# Revit family: Domotics-DomesticRanges-GEWISS-CHORUS_POWER-SOCKET-OUTLET_INDIA_SOUTHAFRICA
name_source: partatom
category: Apparecchi elettrici
revit_build: Autodesk Revit 2016 (Build: 20161004_0715(x64)
units: mm (PartAtom-declared; Revit-internal decimal feet)

## family parameters
Condiviso = Sì
Host = Superficie
Mantenere orientamento annotazione = Sì
Punto di calcolo locali = Sì
Quota connettore circolare = Usa diametro
Taglio con vuoti quando caricato = Sì
Tipo di parte = Normale

## types (3) — shared parameters
Breaking capacity: = 1.25 In (100 position changes)
Carico apparente = 0 VA
Catalogue = DOMOTICS
Catalogue Range = CHORUS - DOMESTIC RANGE
Category = Socket-outlet
Characteristics = With safety shields
Description. = Socket-outlet
Description: = 2P+E - 16A
Electrocod = 0131
For plug pins = Ã˜ 7 mm
Glow Wire Test = 850°C
IDF = 119cc1b2-d397-4b28-b8dc-00e194744bda
IDT = 1dbc6e32-bb70-4510-8419-166b85924e3f
Immagine tipo = GW14298.jpg
Insulation resistance = > 5 MOhm
N. poli = 1
No. Chorus modules = 2
No. Chorus modules: = 2
Produttore = GEWISS S.p.A.
Prolonged operation (no.of position changes) = 10.000 at In 250 V ac cosÃ˜=0,8
Prospetto di default = 1219 mm
Resistance at test voltage = 2000 V at 50 Hz for 1 minute
SEO = Socket outlet
Standard = India/South Africa
Standard: = Indian-South African
Standard; = IEC 60884-1
TXT ELETTRICO = 16
Technical sheet = https://www.gewiss.com
Terminal grip on cable traction = > 50 N
Terminal tightening capacity flexible cables (mm2) = min. 0,75 - max. 2x4
Terminal tightening capacity rigid cables (mm2) = min. 0,5 - max. 2x2,5
Thermo-pressure with ball = 125
Tipo_ = CHORUS PRESE INDIA SUDAFRICA_GENERICO : TITANIO
URL = https://www.gewiss.com
Version file RFA = 19.0
Volt = 230 V
Voltage = 250 V ac
Voltage: = 250 V ac
Wiring terminals = With screw

## per-type parameters (varying)
| type | Colour | Descrizione | EAN code | Modello |
| GW10298 - Socket outlet 2M 2P+E 16A ind/s.afr white | White | S. OUTLET 2M 2P+E 16A IND/S.AFR WH. | 8011564421806 | GW10298 |
| GW14298 - Socket outlet 2P+E 16A d7mm 2M ind/s.afr.st. titanium | Titanium | 2M+E 16A D7MM 2M IND/S.AFR.ST.SOCKET TI. | 8011564421813 | GW14298 |
| GW12298 - Socket outlet 2P+E 16A d7mm 2M ind/s.afr.st.Socket outlet black | Black | 2M+E 16A D7MM 2M IND/S.AFR.ST.SOCKET BL. | 8011564421820 | GW12298 |

note: source unit labels omitted for Thermo-pressure with ball — the stored unit's dimension contradicts the parameter name (converter mislabeling)

## geometry (parser evidence)
native form markers: Sweep x2
no freeform markers — native parametric forms only
